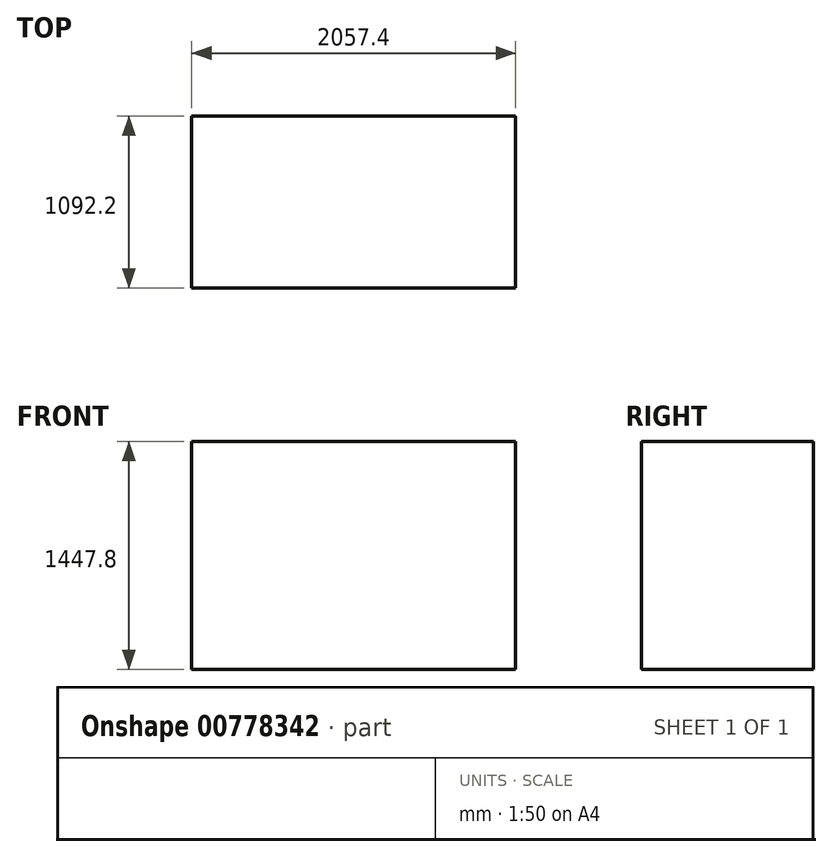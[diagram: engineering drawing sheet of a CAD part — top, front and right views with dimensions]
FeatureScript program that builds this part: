
annotation { "Feature Type Name" : "Feature", "Feature Type Description" : "" }
export const myFeature = defineFeature(function(context is Context, id is Id, definition is map)
    precondition{}
    {
        {
            var Q0;
            Q0=qCreatedBy(makeId("Front.planeOp"),FACE);
            var sketch = newSketch(context, id + "F0", { "sketchPlane" : qUnion([Q0])});
            skLineSegment(sketch, "E0.bottom", {"start": v(0, 0) * mm, "end": v(2057.4, 0) * mm});
            skLineSegment(sketch, "E0.top", {"start": v(0, 1447.8) * mm, "end": v(2057.4, 1447.8) * mm});
            skLineSegment(sketch, "E0.left", {"start": v(0, 0) * mm, "end": v(0, 1447.8) * mm});
            skLineSegment(sketch, "E0.right", {"start": v(2057.4, 0) * mm, "end": v(2057.4, 1447.8) * mm});
            skSolve(sketch);
        }
        {
            var Q0;
            Q0 = qSketchRegion(id + "F0", true);
            extrude(context, id + "F1", {"entities" : qUnion([Q0]), "depth" : 1092.2 * mm, "offsetDistance" : 25.4 * mm});
        }
    });
